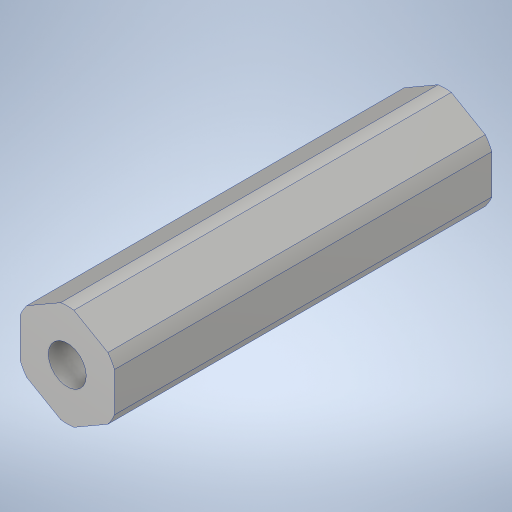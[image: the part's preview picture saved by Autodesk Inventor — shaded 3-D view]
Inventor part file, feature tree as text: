
AUTODESK INVENTOR PART (.ipt)
format: ipt  version: 2023.3 (Build 273359000, 359)  size: 248,320 bytes
history: native  units: in
note: dims shown in document units (in); Inventor stores cm internally (conversion verified against a paired STEP export)
features: sketch x3, extrude x2, projected_geometry x2, hole x1
ambient origin geometry x8: Origin, YZ Plane, XZ Plane, XY Plane, X Axis, Y Axis, Z Axis, Center Point
bodies: Solid1 (feature_tree)
feature tree (8):
  extrude  "Extrusion1"  Depth=1.0in
  hole  "Hole1"  [1 undecoded]
  extrude  "Extrusion3"  [1 undecoded]
  sketch  "Sketch1"  dims[d2=0.0in]
  sketch  "Sketch3"  dims[d9=0.625in d10=0.385in d11=0.25in d12=0.5635in d13=1.0in d14=0.8108in d16=0.7in]
  sketch  "Sketch4"  dims[d17=0.0in d18=0.0in]
  projected_geometry  "Project Cut Edges1"
  projected_geometry  "Project Cut Edges2"
note: 2 required parameter values undecoded (feature->parameter linkage not recoverable at this tier; creation-order binding heuristic only, values carry confidence <= 0.55)
